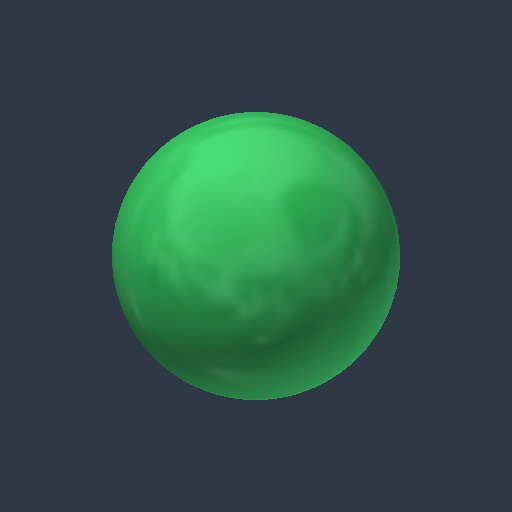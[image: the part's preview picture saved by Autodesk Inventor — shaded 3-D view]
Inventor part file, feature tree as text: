
AUTODESK INVENTOR PART (.ipt)
format: ipt  version: 2024.3 (Build 283343000, 343)  size: 160,256 bytes
history: native  units: mm (DEFAULTED — no unit token found)
features: revolve x1
ambient origin geometry x8: Origin, YZ Plane, XZ Plane, XY Plane, X Axis, Y Axis, Z Axis, Center Point
bodies: Solid1 (feature_tree)
feature tree (1):
  revolve  "Revolve2"  [1 undecoded]
note: 1 required parameter value undecoded (feature->parameter linkage not recoverable at this tier; creation-order binding heuristic only, values carry confidence <= 0.55)
